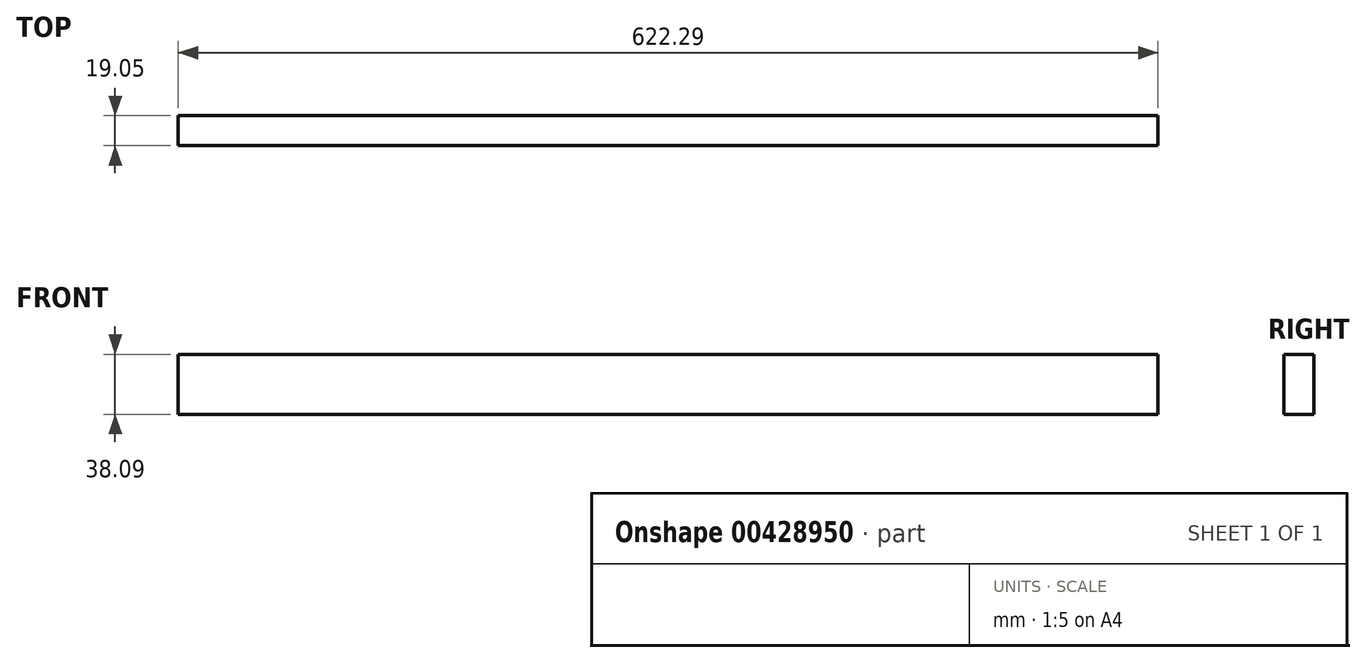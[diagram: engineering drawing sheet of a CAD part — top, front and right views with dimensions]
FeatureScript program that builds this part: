
annotation { "Feature Type Name" : "Feature", "Feature Type Description" : "" }
export const myFeature = defineFeature(function(context is Context, id is Id, definition is map)
    precondition{}
    {
        {
            var Q0;
            Q0=qCreatedBy(makeId("Front.planeOp"),FACE);
            var sketch = newSketch(context, id + "F0", { "sketchPlane" : qUnion([Q0])});
            skLineSegment(sketch, "E0.bottom", {"start": v(-90.6, 32.64) * mm, "end": v(70.45, 32.64) * mm});
            skLineSegment(sketch, "E0.top", {"start": v(-90.6, -15.44) * mm, "end": v(70.45, -15.44) * mm});
            skLineSegment(sketch, "E0.left", {"start": v(-90.6, 32.64) * mm, "end": v(-90.6, -15.44) * mm});
            skLineSegment(sketch, "E0.right", {"start": v(70.45, 32.64) * mm, "end": v(70.45, -15.44) * mm});
            skSolve(sketch);
        }
        {
            var Q0;
            Q0=makeQuery(id+"F0.imprint","IMPRINT",FACE,{"disambiguationData":[TD([[makeQuery(id+"F0.imprint","IMPRINT",EDGE,{"derivedFrom":sQuery(id+"F0.wireOp",EDGE,"E0.bottom")}),-1.0]])]});
            extrude(context, id + "F1", {"entities" : qUnion([Q0]), "depth" : 19.05 * mm});
        }
        {
            var Q0;
            Q0=makeQuery(id+"F1.opExtrude","SWEPT_FACE",FACE,{"disambiguationData":[OSD([sQuery(id+"F0.wireOp",EDGE,"E0.right")])]});
            var sketch = newSketch(context, id + "F2", { "sketchPlane" : qUnion([Q0])});
            skSolve(sketch);
        }
        {
            var Q0;
            {var subQ0=sQuery(id+"F0.wireOp",EDGE,"E0.right");Q0=makeQuery(id+"F2.imprint","IMPRINT",FACE,{"disambiguationData":[TD([[makeQuery(id+"F2.imprint","IMPRINT",EDGE,{"derivedFrom":makeQuery(id+"F1.opExtrude","CAP_EDGE",EDGE,{"disambiguationData":[OSD([subQ0])],"isStart":true})}),-1.0]])]});}
            extrude(context, id + "F3", {"entities" : qUnion([Q0]), "operationType" : NewBodyOperationType.ADD, "depth" : 622.3 * mm});
        }
        {
            var Q0;
            Q0=makeQuery(id+"F3.opExtrude","CAP_FACE",FACE,{"disambiguationData":[OSD([sQuery(id+"F0.wireOp",EDGE,"E0.bottom"),sQuery(id+"F0.wireOp",EDGE,"E0.top"),sQuery(id+"F0.wireOp",EDGE,"E0.right")])],"isStart":false});
            extrude(context, id + "F4", {"entities" : qUnion([Q0]), "operationType" : NewBodyOperationType.REMOVE, "oppositeDirection" : true, "depth" : 161.06 * mm});
        }
        {
            var Q0;
            {var subQ0=sQuery(id+"F0.wireOp",EDGE,"E0.top");Q0=makeQuery(id+"F3.boolean.opBoolean","MERGE",FACE,{"derivedFrom":[makeQuery(id+"F1.opExtrude","SWEPT_FACE",FACE,{"disambiguationData":[OSD([subQ0])]}),makeQuery(id+"F3.opExtrude","SWEPT_FACE",FACE,{"disambiguationData":[OSD([subQ0,sQuery(id+"F0.wireOp",EDGE,"E0.right")])]})]});}
            extrude(context, id + "F5", {"entities" : qUnion([Q0]), "operationType" : NewBodyOperationType.REMOVE, "oppositeDirection" : true, "depth" : 9.98 * mm});
        }
    });
